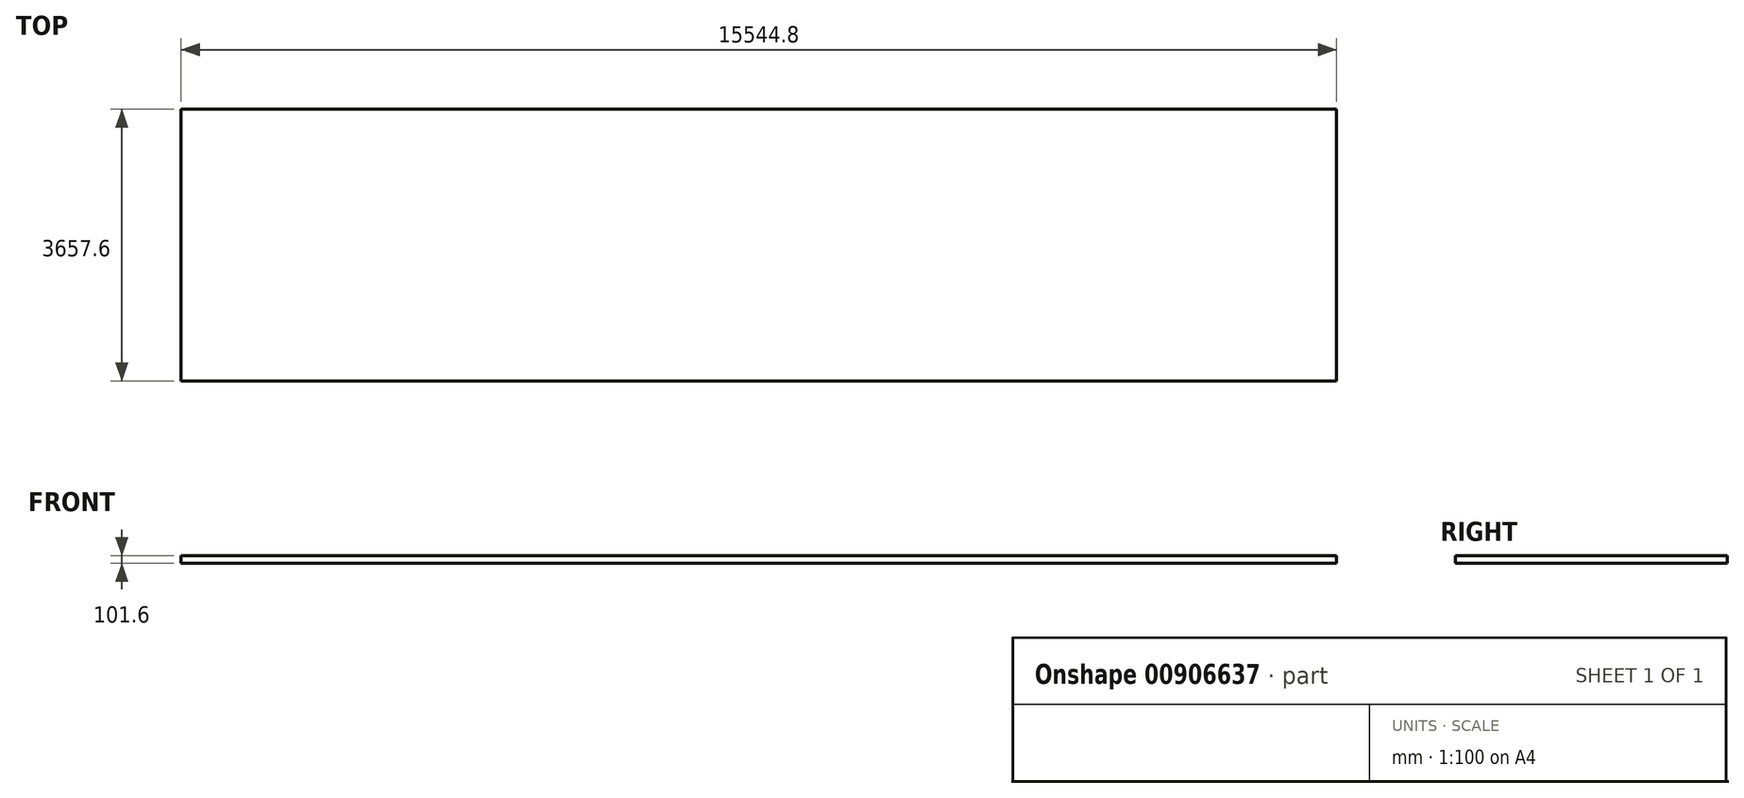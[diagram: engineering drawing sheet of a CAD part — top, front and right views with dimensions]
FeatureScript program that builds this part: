
annotation { "Feature Type Name" : "Feature", "Feature Type Description" : "" }
export const myFeature = defineFeature(function(context is Context, id is Id, definition is map)
    precondition{}
    {
        {
            var Q0;
            Q0=qCreatedBy(makeId("Top.planeOp"),FACE);
            var sketch = newSketch(context, id + "F0", { "sketchPlane" : qUnion([Q0])});
            skLineSegment(sketch, "E0.bottom", {"start": v(7772.4, -1828.8) * mm, "end": v(-7772.4, -1828.8) * mm});
            skLineSegment(sketch, "E0.top", {"start": v(7772.4, 1828.8) * mm, "end": v(-7772.4, 1828.8) * mm});
            skLineSegment(sketch, "E0.left", {"start": v(7772.4, -1828.8) * mm, "end": v(7772.4, 1828.8) * mm});
            skLineSegment(sketch, "E0.right", {"start": v(-7772.4, -1828.8) * mm, "end": v(-7772.4, 1828.8) * mm});
            skPoint(sketch, "E0.middle", {"position": v(0, 0) * mm});
            skSolve(sketch);
        }
        {
            var Q0;
            Q0=makeQuery(id+"F0.imprint","IMPRINT",FACE,{"disambiguationData":[TD([[makeQuery(id+"F0.imprint","IMPRINT",EDGE,{"derivedFrom":sQuery(id+"F0.wireOp",EDGE,"E0.bottom")}),-1.0]])]});
            extrude(context, id + "F1", {"entities" : qUnion([Q0]), "depth" : 101.6 * mm, "offsetDistance" : 25.4 * mm});
        }
    });
